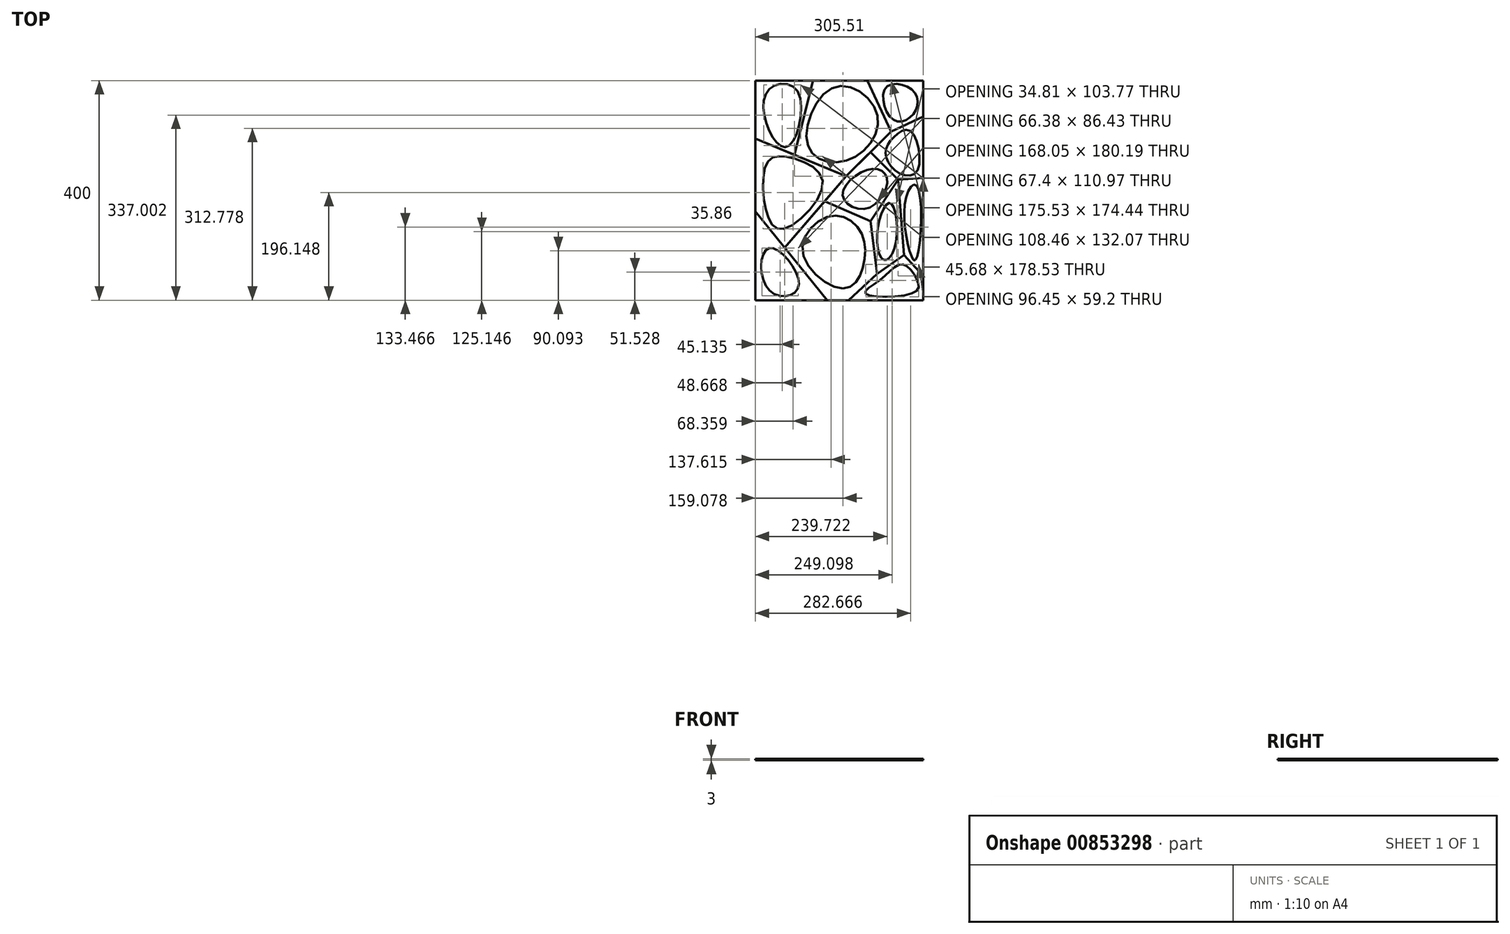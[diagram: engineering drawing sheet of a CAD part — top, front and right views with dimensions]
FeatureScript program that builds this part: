
annotation { "Feature Type Name" : "Feature", "Feature Type Description" : "" }
export const myFeature = defineFeature(function(context is Context, id is Id, definition is map)
    precondition{}
    {
        {
            var Q0;
            Q0=qCreatedBy(makeId("Top.planeOp"),FACE);
            var sketch = newSketch(context, id + "F0", { "sketchPlane" : qUnion([Q0])});
            skLineSegment(sketch, "E0.bottom", {"start": v(0, 0) * mm, "end": v(305.5, 0) * mm});
            skLineSegment(sketch, "E0.top", {"start": v(0, 400) * mm, "end": v(305.5, 400) * mm});
            skLineSegment(sketch, "E0.left", {"start": v(0, 0) * mm, "end": v(0, 400) * mm});
            skLineSegment(sketch, "E0.right", {"start": v(305.5, 0) * mm, "end": v(305.5, 400) * mm});
            skLineSegment(sketch, "E1", {"start": v(130.73, 0) * mm, "end": v(0, 161.97) * mm});
            skLineSegment(sketch, "E2", {"start": v(53.6, 95.57) * mm, "end": v(165.29, 225.56) * mm});
            skLineSegment(sketch, "E3", {"start": v(165.29, 225.56) * mm, "end": v(0, 294.67) * mm});
            skLineSegment(sketch, "E4", {"start": v(71.31, 264.85) * mm, "end": v(104.47, 400) * mm});
            skLineSegment(sketch, "E5", {"start": v(165.29, 225.56) * mm, "end": v(246.84, 307.11) * mm});
            skLineSegment(sketch, "E6", {"start": v(246.84, 307.11) * mm, "end": v(204, 400) * mm});
            skLineSegment(sketch, "E7", {"start": v(169.43, 0) * mm, "end": v(221.64, 47.91) * mm});
            skLineSegment(sketch, "E8", {"start": v(221.64, 47.91) * mm, "end": v(209.39, 144.25) * mm});
            skLineSegment(sketch, "E9", {"start": v(209.39, 144.25) * mm, "end": v(126.3, 180.19) * mm});
            skLineSegment(sketch, "E10", {"start": v(209.39, 144.25) * mm, "end": v(259.82, 219.22) * mm});
            skLineSegment(sketch, "E11", {"start": v(259.82, 219.22) * mm, "end": v(209.39, 269.66) * mm});
            skFitSpline(sketch, "E12", {"points": [v(51.67, 130.11) * mm, v(21.04, 157.81) * mm, v(22.27, 251.5) * mm, v(63.87, 259.72) * mm, v(122.57, 214.39) * mm, v(51.67, 130.11) * mm]});
            skFitSpline(sketch, "E13", {"points": [v(61.62, 281.52) * mm, v(29.67, 300) * mm, v(23.5, 382.6) * mm, v(75.84, 381.9) * mm, v(61.62, 281.52) * mm]});
            skFitSpline(sketch, "E14", {"points": [v(95.8, 281.47) * mm, v(145.23, 388.37) * mm, v(222.32, 335.4) * mm, v(168.06, 255.03) * mm, v(95.8, 281.47) * mm]});
            skPoint(sketch, "E15", {"position": v(178.15, 386.19) * mm});
            skFitSpline(sketch, "E16", {"points": [v(25.26, 94.74) * mm, v(78.72, 25.2) * mm, v(25.14, 18.15) * mm, v(25.26, 94.74) * mm]});
            skPoint(sketch, "E17", {"position": v(37, 92.76) * mm});
            skPoint(sketch, "E18", {"position": v(17.32, 88.83) * mm});
            skPoint(sketch, "E19", {"position": v(75.78, 46.75) * mm});
            skPoint(sketch, "E20", {"position": v(68.94, 12.11) * mm});
            skLineSegment(sketch, "E21", {"start": v(221.64, 47.91) * mm, "end": v(270.32, 82.54) * mm});
            skLineSegment(sketch, "E22", {"start": v(270.32, 82.54) * mm, "end": v(305.5, 44.2) * mm});
            skLineSegment(sketch, "E23", {"start": v(259.82, 219.22) * mm, "end": v(270.32, 82.54) * mm});
            skLineSegment(sketch, "E24", {"start": v(246.84, 307.11) * mm, "end": v(305.5, 334.18) * mm});
            skLineSegment(sketch, "E25", {"start": v(259.82, 219.22) * mm, "end": v(305.5, 222.73) * mm});
            skFitSpline(sketch, "E26", {"points": [v(159.51, 21.47) * mm, v(85.86, 87.89) * mm, v(135.76, 153) * mm, v(190.59, 126.46) * mm, v(195.15, 57.96) * mm, v(159.51, 21.47) * mm]});
            skFitSpline(sketch, "E27", {"points": [v(159.02, 191.24) * mm, v(207.41, 238.12) * mm, v(239.9, 221.44) * mm, v(203.35, 167.15) * mm, v(159.02, 191.24) * mm]});
            skFitSpline(sketch, "E28", {"points": [v(233.44, 73.26) * mm, v(222.94, 133.54) * mm, v(245.77, 176.93) * mm, v(254.82, 100.67) * mm, v(233.44, 73.26) * mm]});
            skFitSpline(sketch, "E29", {"points": [v(237.1, 268.26) * mm, v(252.62, 297.94) * mm, v(282.22, 308) * mm, v(294.18, 234.92) * mm, v(258.56, 233.1) * mm, v(237.1, 268.26) * mm]});
            skFitSpline(sketch, "E30", {"points": [v(251.25, 328.54) * mm, v(237.1, 386.53) * mm, v(286.87, 381.97) * mm, v(288.62, 340.88) * mm, v(251.25, 328.54) * mm]});
            skFitSpline(sketch, "E31", {"points": [v(280.7, 89.27) * mm, v(276.36, 194.63) * mm, v(294.28, 208.2) * mm, v(292.1, 74.07) * mm, v(280.7, 89.27) * mm]});
            skFitSpline(sketch, "E32", {"points": [v(200.87, 12.16) * mm, v(229.65, 39.31) * mm, v(268.21, 65.38) * mm, v(294.82, 36.05) * mm, v(289.4, 14.33) * mm, v(200.87, 12.16) * mm]});
            skSolve(sketch);
        }
        {
            var Q0;
            Q0=makeQuery(id+"F0.imprint","IMPRINT",FACE,{"disambiguationData":[TD([[makeQuery(id+"F0.imprint","IMPRINT",EDGE,{"derivedFrom":sQuery(id+"F0.wireOp",EDGE,"E12")}),1.0]])]});
            extrude(context, id + "F1", {"entities" : qUnion([Q0]), "depth" : 3 * mm, "offsetDistance" : 25 * mm});
        }
        {
            var Q0;
            {var subQ0=sQuery(id+"F0.wireOp",EDGE,"E4");Q0=makeQuery(id+"F0.imprint","IMPRINT",FACE,{"disambiguationData":[TD([[makeQuery(id+"F0.imprint","IMPRINT",EDGE,{"derivedFrom":subQ0}),1.0]])]});}
            extrude(context, id + "F2", {"entities" : qUnion([Q0]), "depth" : 3 * mm, "offsetDistance" : 25 * mm});
        }
        {
            var Q0;
            {var subQ4=sQuery(id+"F0.wireOp",EDGE,"E4");Q0=makeQuery(id+"F0.imprint","IMPRINT",FACE,{"disambiguationData":[TD([[makeQuery(id+"F0.imprint","IMPRINT",EDGE,{"derivedFrom":subQ4}),-1.0]])]});}
            extrude(context, id + "F3", {"entities" : qUnion([Q0]), "depth" : 3 * mm, "offsetDistance" : 25 * mm});
        }
        {
            var Q0;
            Q0=makeQuery(id+"F0.imprint","IMPRINT",FACE,{"disambiguationData":[TD([[makeQuery(id+"F0.imprint","IMPRINT",EDGE,{"derivedFrom":sQuery(id+"F0.wireOp",EDGE,"E16")}),1.0]])]});
            extrude(context, id + "F4", {"entities" : qUnion([Q0]), "depth" : 3 * mm, "offsetDistance" : 25 * mm});
        }
        {
            var Q0;
            {var subQ4=sQuery(id+"F0.wireOp",EDGE,"E7");Q0=makeQuery(id+"F0.imprint","IMPRINT",FACE,{"disambiguationData":[TD([[makeQuery(id+"F0.imprint","IMPRINT",EDGE,{"derivedFrom":subQ4}),1.0]])]});}
            extrude(context, id + "F5", {"entities" : qUnion([Q0]), "depth" : 3 * mm, "offsetDistance" : 25 * mm});
        }
        {
            var Q0;
            {var subQ0=sQuery(id+"F0.wireOp",EDGE,"E9");Q0=makeQuery(id+"F0.imprint","IMPRINT",FACE,{"disambiguationData":[TD([[makeQuery(id+"F0.imprint","IMPRINT",EDGE,{"derivedFrom":subQ0}),-1.0]])]});}
            extrude(context, id + "F6", {"entities" : qUnion([Q0]), "depth" : 3 * mm, "offsetDistance" : 25 * mm});
        }
        {
            var Q0;
            Q0=makeQuery(id+"F0.imprint","IMPRINT",FACE,{"disambiguationData":[TD([[makeQuery(id+"F0.imprint","IMPRINT",EDGE,{"derivedFrom":sQuery(id+"F0.wireOp",EDGE,"E8")}),-1.0]])]});
            extrude(context, id + "F7", {"entities" : qUnion([Q0]), "depth" : 3 * mm, "offsetDistance" : 25 * mm});
        }
        {
            var Q0;
            {var subQ0=sQuery(id+"F0.wireOp",EDGE,"E7");Q0=makeQuery(id+"F0.imprint","IMPRINT",FACE,{"disambiguationData":[TD([[makeQuery(id+"F0.imprint","IMPRINT",EDGE,{"derivedFrom":subQ0}),-1.0]])]});}
            extrude(context, id + "F8", {"entities" : qUnion([Q0]), "depth" : 3 * mm, "offsetDistance" : 25 * mm});
        }
        {
            var Q0;
            {var subQ1=sQuery(id+"F0.wireOp",EDGE,"E11");Q0=makeQuery(id+"F0.imprint","IMPRINT",FACE,{"disambiguationData":[TD([[makeQuery(id+"F0.imprint","IMPRINT",EDGE,{"derivedFrom":subQ1}),-1.0]])]});}
            extrude(context, id + "F9", {"entities" : qUnion([Q0]), "depth" : 3 * mm, "offsetDistance" : 25 * mm});
        }
        {
            var Q0;
            {var subQ1=sQuery(id+"F0.wireOp",EDGE,"E22");Q0=makeQuery(id+"F0.imprint","IMPRINT",FACE,{"disambiguationData":[TD([[makeQuery(id+"F0.imprint","IMPRINT",EDGE,{"derivedFrom":subQ1}),1.0]])]});}
            extrude(context, id + "F10", {"entities" : qUnion([Q0]), "depth" : 3 * mm, "offsetDistance" : 25 * mm});
        }
        {
            var Q0;
            {var subQ0=sQuery(id+"F0.wireOp",EDGE,"E6");Q0=makeQuery(id+"F0.imprint","IMPRINT",FACE,{"disambiguationData":[TD([[makeQuery(id+"F0.imprint","IMPRINT",EDGE,{"derivedFrom":subQ0}),-1.0]])]});}
            extrude(context, id + "F11", {"entities" : qUnion([Q0]), "depth" : 3 * mm, "offsetDistance" : 25 * mm});
        }
    });
